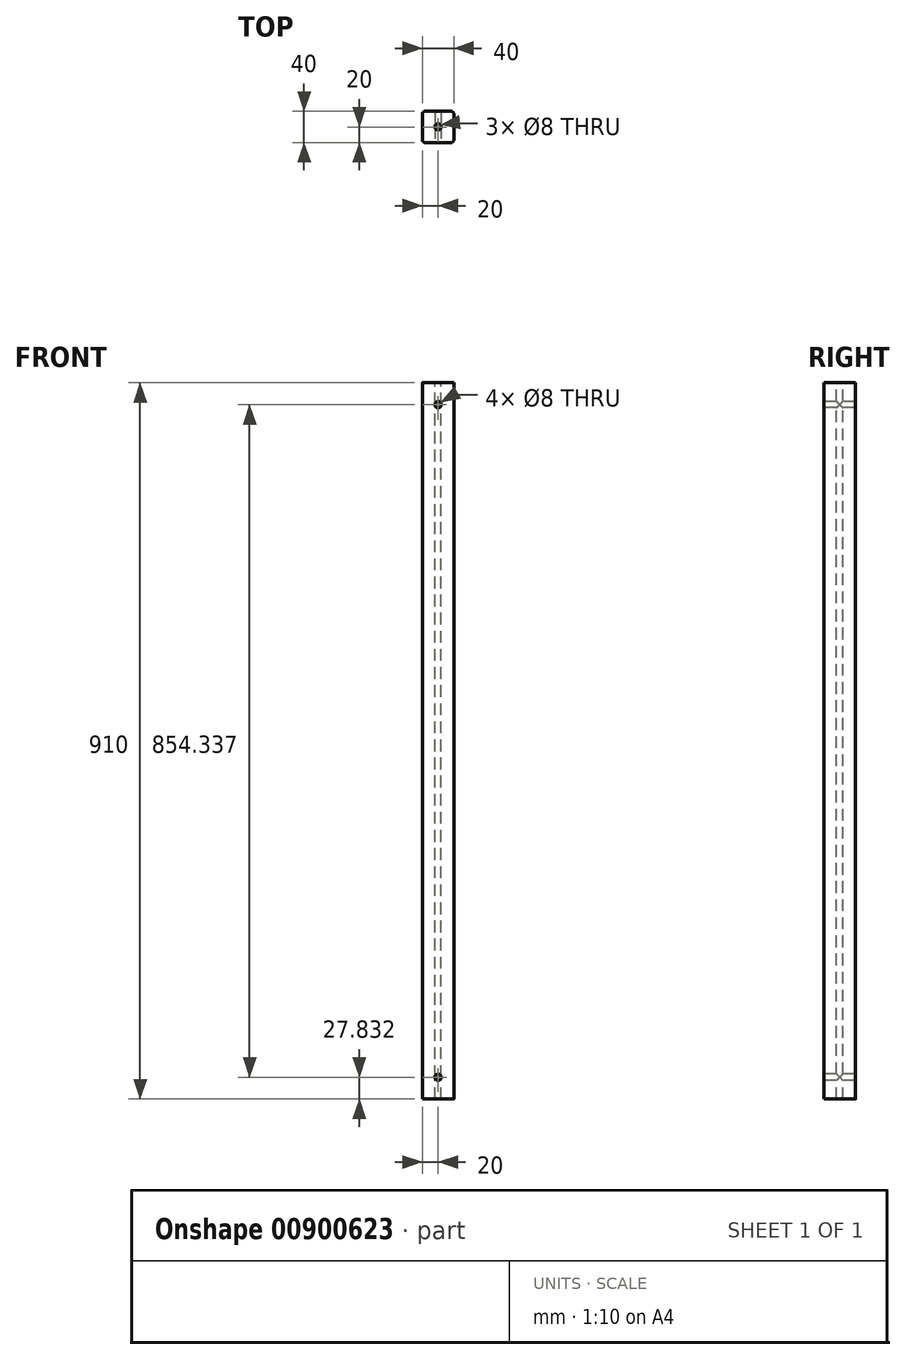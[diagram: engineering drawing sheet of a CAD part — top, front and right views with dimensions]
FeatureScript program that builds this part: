
annotation { "Feature Type Name" : "Feature", "Feature Type Description" : "" }
export const myFeature = defineFeature(function(context is Context, id is Id, definition is map)
    precondition{}
    {
        {
            var Q0;
            Q0=qCreatedBy(makeId("Top.planeOp"),FACE);
            var sketch = newSketch(context, id + "F0", { "sketchPlane" : qUnion([Q0])});
            skLineSegment(sketch, "E0.bottom", {"start": v(20, -20) * mm, "end": v(-20, -20) * mm});
            skLineSegment(sketch, "E0.top", {"start": v(20, 20) * mm, "end": v(-20, 20) * mm});
            skLineSegment(sketch, "E0.left", {"start": v(20, -20) * mm, "end": v(20, 20) * mm});
            skLineSegment(sketch, "E0.right", {"start": v(-20, -20) * mm, "end": v(-20, 20) * mm});
            skPoint(sketch, "E0.middle", {"position": v(0, 0) * mm});
            skSolve(sketch);
        }
        {
            var Q0;
            Q0=makeQuery(id+"F0.imprint","IMPRINT",FACE,{"disambiguationData":[TD([[makeQuery(id+"F0.imprint","IMPRINT",EDGE,{"derivedFrom":sQuery(id+"F0.wireOp",EDGE,"E0.bottom")}),-1.0]])]});
            extrude(context, id + "F1", {"entities" : qUnion([Q0]), "depth" : 910 * mm, "offsetDistance" : 25 * mm});
        }
        {
            var Q0;
            Q0=makeQuery(id+"F1.opExtrude","CAP_FACE",FACE,{"disambiguationData":[OSD([sQuery(id+"F0.wireOp",EDGE,"E0.bottom"),sQuery(id+"F0.wireOp",EDGE,"E0.top"),sQuery(id+"F0.wireOp",EDGE,"E0.left"),sQuery(id+"F0.wireOp",EDGE,"E0.right")])],"isStart":false});
            var sketch = newSketch(context, id + "F2", { "sketchPlane" : qUnion([Q0])});
            skPoint(sketch, "E1", {"position": v(0, 0) * mm});
            skSolve(sketch);
        }
        {
            var Q0;
            Q0=sQuery(id+"F2.wireOp",VERTEX,"E1");
            var Q1;
            Q1=makeQuery(id+"F1.opExtrude","SWEPT_BODY",BODY,{"disambiguationData":[OSD([sQuery(id+"F0.wireOp",EDGE,"E0.bottom"),sQuery(id+"F0.wireOp",EDGE,"E0.top"),sQuery(id+"F0.wireOp",EDGE,"E0.left"),sQuery(id+"F0.wireOp",EDGE,"E0.right")])]});
            hole(context, id + "F3", {"style" : HoleStyle.SIMPLE, "endStyle" : HoleEndStyle.THROUGH, "holeDiameter" : 8 * mm, "majorDiameter" : 5 * mm, "isTappedThrough" : true, "tappedDepth" : 12 * mm, "tapClearance" : 3, "locations" : qUnion([Q0]), "scope" : qUnion([Q1])});
        }
        {
            var Q0;
            Q0=makeQuery(id+"F1.opExtrude","SWEPT_EDGE",EDGE,{"disambiguationData":[OSD([sQuery(id+"F0.wireOp",EDGE,"E0.bottom"),sQuery(id+"F0.wireOp",EDGE,"E0.right")])]});
            var Q1;
            Q1=makeQuery(id+"F1.opExtrude","SWEPT_EDGE",EDGE,{"disambiguationData":[OSD([sQuery(id+"F0.wireOp",EDGE,"E0.bottom"),sQuery(id+"F0.wireOp",EDGE,"E0.left")])]});
            var Q2;
            Q2=makeQuery(id+"F1.opExtrude","SWEPT_EDGE",EDGE,{"disambiguationData":[OSD([sQuery(id+"F0.wireOp",EDGE,"E0.top"),sQuery(id+"F0.wireOp",EDGE,"E0.left")])]});
            var Q3;
            Q3=makeQuery(id+"F1.opExtrude","SWEPT_EDGE",EDGE,{"disambiguationData":[OSD([sQuery(id+"F0.wireOp",EDGE,"E0.top"),sQuery(id+"F0.wireOp",EDGE,"E0.right")])]});
            fillet(context, id + "F4", {"entities" : qUnion([Q0, Q1, Q2, Q3]), "radius" : 4 * mm, "tangentPropagation" : true, "allowEdgeOverflow" : false});
        }
        {
            var Q0;
            Q0=makeQuery(id+"F1.opExtrude","SWEPT_FACE",FACE,{"disambiguationData":[OSD([sQuery(id+"F0.wireOp",EDGE,"E0.bottom")])]});
            var sketch = newSketch(context, id + "F5", { "sketchPlane" : qUnion([Q0])});
            skCircle(sketch, "E2", {"center": v(0, 882.17) * mm, "radius": 4 * mm});
            skCircle(sketch, "E3", {"center": v(0, 27.83) * mm, "radius": 4 * mm});
            skSolve(sketch);
        }
        {
            var Q0;
            Q0=sQuery(id+"F5.wireOp",VERTEX,"E3.center");
            var Q1;
            Q1=sQuery(id+"F5.wireOp",VERTEX,"E2.center");
            var Q2;
            Q2=makeQuery(id+"F1.opExtrude","SWEPT_BODY",BODY,{"disambiguationData":[OSD([sQuery(id+"F0.wireOp",EDGE,"E0.bottom"),sQuery(id+"F0.wireOp",EDGE,"E0.top"),sQuery(id+"F0.wireOp",EDGE,"E0.left"),sQuery(id+"F0.wireOp",EDGE,"E0.right")])]});
            hole(context, id + "F6", {"style" : HoleStyle.SIMPLE, "endStyle" : HoleEndStyle.THROUGH, "holeDiameter" : 8 * mm, "majorDiameter" : 5 * mm, "isTappedThrough" : true, "tappedDepth" : 12 * mm, "tapClearance" : 3, "locations" : qUnion([Q0, Q1]), "scope" : qUnion([Q2])});
        }
    });
